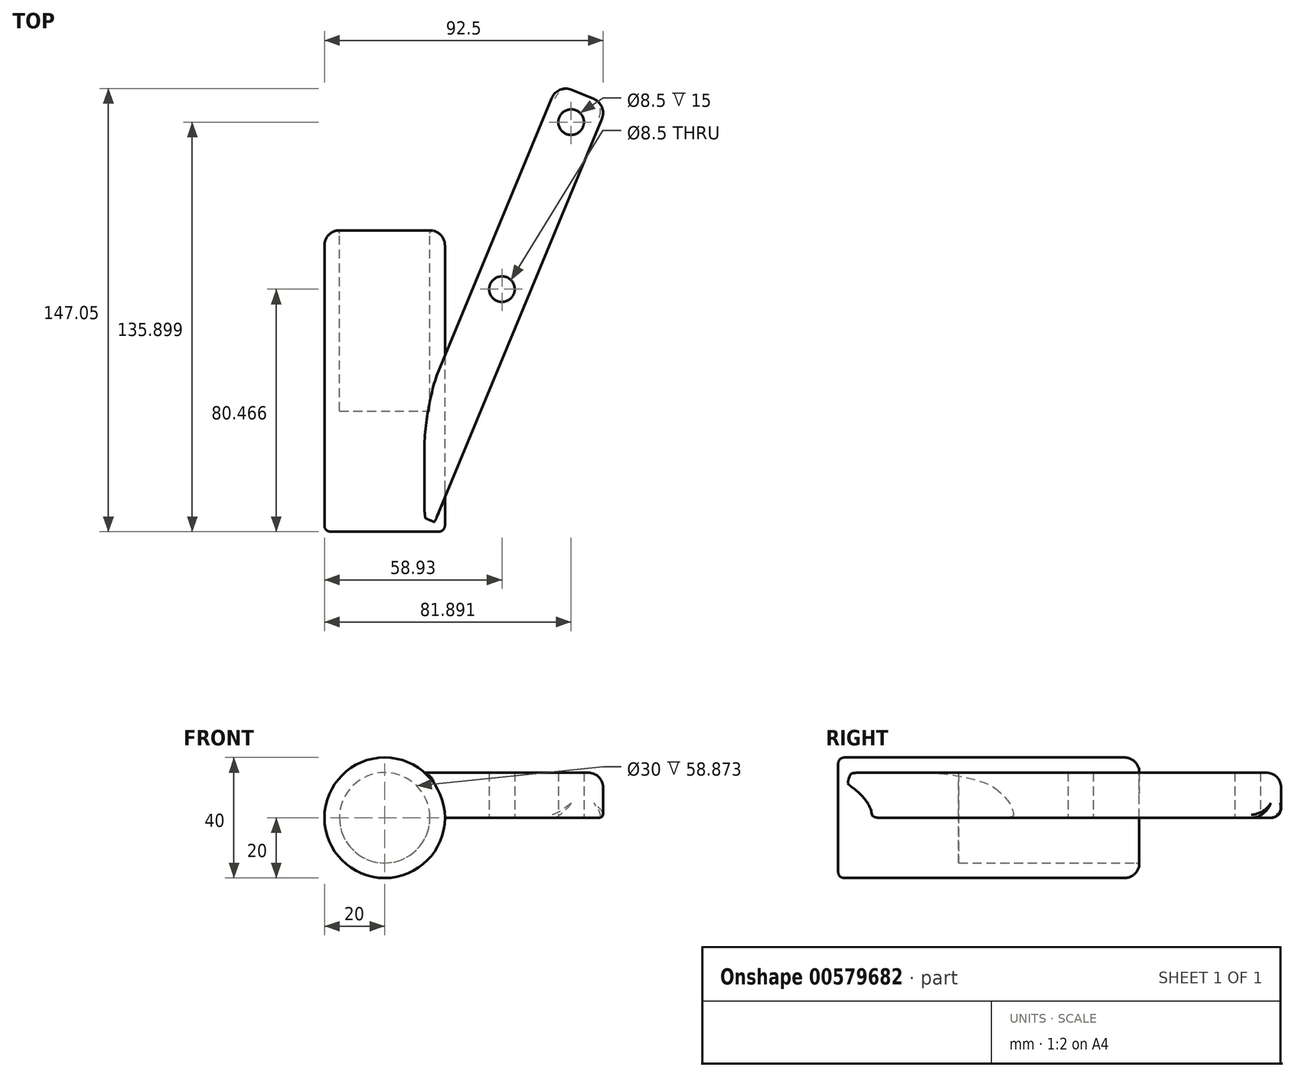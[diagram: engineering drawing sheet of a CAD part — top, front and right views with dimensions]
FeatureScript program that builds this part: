
annotation { "Feature Type Name" : "Feature", "Feature Type Description" : "" }
export const myFeature = defineFeature(function(context is Context, id is Id, definition is map)
    precondition{}
    {
        {
            var Q0;
            Q0=qCreatedBy(makeId("Top.planeOp"),FACE);
            var sketch = newSketch(context, id + "F0", { "sketchPlane" : qUnion([Q0])});
            skLineSegment(sketch, "E0.bottom", {"start": v(20, -10) * mm, "end": v(-20, -10) * mm});
            skLineSegment(sketch, "E0.top", {"start": v(20, 90) * mm, "end": v(-20, 90) * mm});
            skLineSegment(sketch, "E0.left", {"start": v(20, -10) * mm, "end": v(20, 90) * mm});
            skLineSegment(sketch, "E0.right", {"start": v(-20, -10) * mm, "end": v(-20, 90) * mm});
            skPoint(sketch, "E0.middle", {"position": v(0, 0) * mm});
            skLineSegment(sketch, "E1.bottom", {"start": v(0, 0) * mm, "end": v(16.63, -6.89) * mm});
            skLineSegment(sketch, "E1.top", {"start": v(57.4, 138.58) * mm, "end": v(74.03, 131.7) * mm});
            skLineSegment(sketch, "E1.left", {"start": v(0, 0) * mm, "end": v(57.4, 138.58) * mm});
            skLineSegment(sketch, "E1.right", {"start": v(16.63, -6.89) * mm, "end": v(74.03, 131.7) * mm});
            skCircle(sketch, "E2", {"center": v(61.9, 125.9) * mm, "radius": 4.25 * mm});
            skCircle(sketch, "E3", {"center": v(38.93, 70.47) * mm, "radius": 4.25 * mm});
            skLineSegment(sketch, "E4", {"start": v(0, 90) * mm, "end": v(0, -10) * mm});
            skPoint(sketch, "E5", {"position": v(0, 90) * mm});
            skSolve(sketch);
        }
        {
            var Q0;
            {var subQ5=sQuery(id+"F0.wireOp",EDGE,"E1.bottom");Q0=makeQuery(id+"F0.imprint","IMPRINT",FACE,{"disambiguationData":[TD([[makeQuery(id+"F0.imprint","IMPRINT",EDGE,{"derivedFrom":subQ5}),1.0]])]});}
            var Q1;
            {var subQ1=sQuery(id+"F0.wireOp",EDGE,"E1.top");Q1=makeQuery(id+"F0.imprint","IMPRINT",FACE,{"disambiguationData":[TD([[makeQuery(id+"F0.imprint","IMPRINT",EDGE,{"derivedFrom":subQ1}),-1.0]])]});}
            extrude(context, id + "F1", {"entities" : qUnion([Q0, Q1]), "depth" : 15 * mm, "offsetDistance" : 25 * mm});
        }
        {
            var Q0;
            {var subQ0=sQuery(id+"F0.wireOp",EDGE,"E0.right");Q0=makeQuery(id+"F0.imprint","IMPRINT",FACE,{"disambiguationData":[TD([[makeQuery(id+"F0.imprint","IMPRINT",EDGE,{"derivedFrom":subQ0}),-1.0]])]});}
            var Q1;
            Q1=sQuery(id+"F0.wireOp",EDGE,"E4");
            revolve(context, id + "F2", {"operationType" : NewBodyOperationType.ADD, "entities" : qUnion([Q0]), "axis" : qUnion([Q1]), "revolveType" : RevolveType.FULL});
        }
        {
            var Q0;
            Q0=makeQuery(id+"F1.opExtrude","CAP_EDGE",EDGE,{"disambiguationData":[OSD([sQuery(id+"F0.wireOp",EDGE,"E1.left")])],"isStart":false});
            var Q1;
            Q1=makeQuery(id+"F1.opExtrude","CAP_EDGE",EDGE,{"disambiguationData":[OSD([sQuery(id+"F0.wireOp",EDGE,"E1.right")])],"isStart":false});
            fillet(context, id + "F3", {"entities" : qUnion([Q0, Q1]), "radius" : 5 * mm, "tangentPropagation" : true, "allowEdgeOverflow" : false});
        }
        {
            var Q0;
            Q0=makeQuery(id+"F1.opExtrude","CAP_EDGE",EDGE,{"disambiguationData":[OSD([sQuery(id+"F0.wireOp",EDGE,"E1.left")])],"isStart":true});
            var Q1;
            Q1=makeQuery(id+"F1.opExtrude","CAP_EDGE",EDGE,{"disambiguationData":[OSD([sQuery(id+"F0.wireOp",EDGE,"E1.right")])],"isStart":true});
            fillet(context, id + "F4", {"entities" : qUnion([Q0, Q1]), "radius" : 1 * mm, "tangentPropagation" : true, "allowEdgeOverflow" : false});
        }
        {
            var Q0;
            Q0=makeQuery(id+"F1.opExtrude","SWEPT_FACE",FACE,{"disambiguationData":[OSD([sQuery(id+"F0.wireOp",EDGE,"E1.top")])]});
            fillet(context, id + "F5", {"entities" : qUnion([Q0]), "radius" : 5 * mm, "tangentPropagation" : true, "allowEdgeOverflow" : false});
        }
        {
            var Q0;
            Q0=makeQuery(id+"F2.opRevolve","SWEPT_FACE",FACE,{"disambiguationData":[OSD([sQuery(id+"F0.wireOp",EDGE,"E0.top")])]});
            fillet(context, id + "F6", {"entities" : qUnion([Q0]), "radius" : 5 * mm, "tangentPropagation" : true, "allowEdgeOverflow" : false});
        }
        {
            var Q0;
            Q0=makeQuery(id+"F2.opRevolve","SWEPT_FACE",FACE,{"disambiguationData":[OSD([sQuery(id+"F0.wireOp",EDGE,"E0.bottom")])]});
            fillet(context, id + "F7", {"entities" : qUnion([Q0]), "radius" : 2 * mm, "tangentPropagation" : true, "allowEdgeOverflow" : false});
        }
        {
            var Q0;
            Q0=makeQuery(id+"F2.opRevolve","SWEPT_FACE",FACE,{"disambiguationData":[OSD([sQuery(id+"F0.wireOp",EDGE,"E0.top")])]});
            extrude(context, id + "F8", {"entities" : qUnion([Q0]), "operationType" : NewBodyOperationType.REMOVE, "oppositeDirection" : true, "depth" : 60 * mm, "offsetDistance" : 25 * mm});
        }
        {
            var Q0;
            {var subQ0=sQuery(id+"F0.wireOp",EDGE,"E0.right");var subQ1=sQuery(id+"F0.wireOp",EDGE,"E0.top");Q0=makeQuery(id+"F8.boolean.opBoolean","MERGE",EDGE,{"derivedFrom":[makeQuery(id+"F6.opFillet","BLEND_EDGE",EDGE,{"blendedFrom":[makeQuery(id+"F2.opRevolve","SWEPT_EDGE",EDGE,{"disambiguationData":[OSD([subQ1,subQ0])]}),makeQuery(id+"F2.opRevolve","SWEPT_FACE",FACE,{"disambiguationData":[OSD([subQ1])]})],"blendedInto":[makeQuery(id+"F2.opRevolve","SWEPT_FACE",FACE,{"disambiguationData":[OSD([subQ1])]})]}),makeQuery(id+"F8.opExtrude","CAP_EDGE",EDGE,{"disambiguationData":[OSD([subQ1,subQ0])],"isStart":true})]});}
            fillet(context, id + "F9", {"entities" : qUnion([Q0]), "radius" : 1 * mm, "tangentPropagation" : true, "allowEdgeOverflow" : false});
        }
    });
